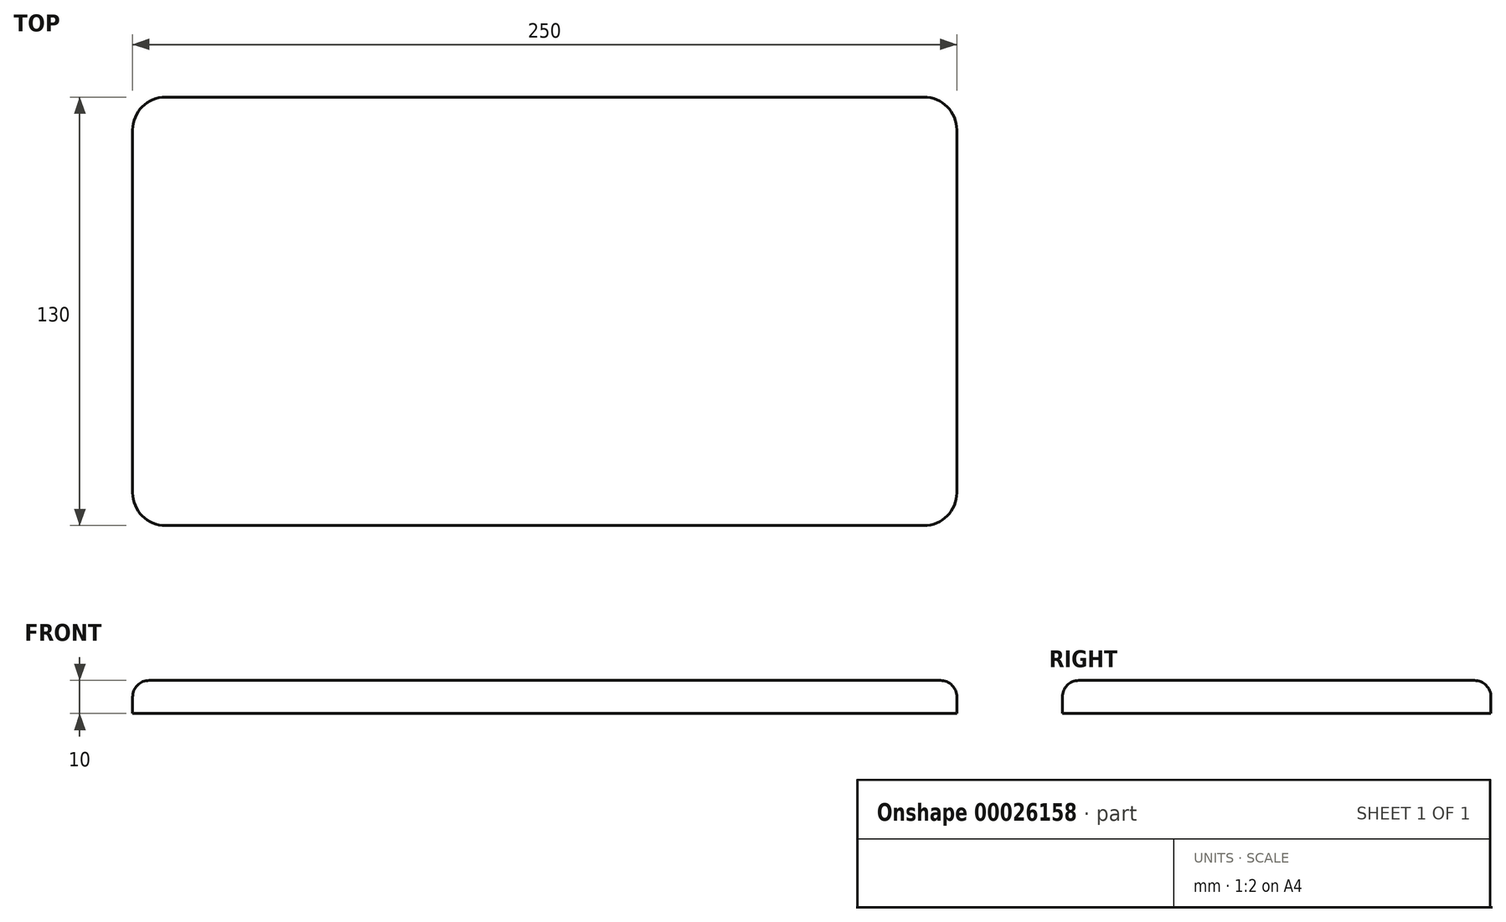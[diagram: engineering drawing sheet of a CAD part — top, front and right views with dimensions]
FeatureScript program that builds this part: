
annotation { "Feature Type Name" : "Feature", "Feature Type Description" : "" }
export const myFeature = defineFeature(function(context is Context, id is Id, definition is map)
    precondition{}
    {
        {
            var Q0;
            Q0=qCreatedBy(makeId("Top.planeOp"),FACE);
            var sketch = newSketch(context, id + "F0", { "sketchPlane" : qUnion([Q0])});
            skLineSegment(sketch, "E0.bottom", {"start": v(-167.36, 72.19) * mm, "end": v(82.64, 72.19) * mm});
            skLineSegment(sketch, "E0.top", {"start": v(-167.36, -57.81) * mm, "end": v(82.64, -57.81) * mm});
            skLineSegment(sketch, "E0.left", {"start": v(-167.36, 72.19) * mm, "end": v(-167.36, -57.81) * mm});
            skLineSegment(sketch, "E0.right", {"start": v(82.64, 72.19) * mm, "end": v(82.64, -57.81) * mm});
            skSolve(sketch);
        }
        {
            var Q0;
            Q0=makeQuery(id+"F0.imprint","IMPRINT",FACE,{"disambiguationData":[TD([[makeQuery(id+"F0.imprint","IMPRINT",EDGE,{"derivedFrom":sQuery(id+"F0.wireOp",EDGE,"E0.bottom")}),-1.0]])]});
            extrude(context, id + "F1", {"entities" : qUnion([Q0]), "depth" : 10 * mm});
        }
        {
            var Q0;
            Q0=makeQuery(id+"F1.opExtrude","SWEPT_EDGE",EDGE,{"disambiguationData":[OSD([sQuery(id+"F0.wireOp",EDGE,"E0.top"),sQuery(id+"F0.wireOp",EDGE,"E0.right")])]});
            var Q1;
            Q1=makeQuery(id+"F1.opExtrude","SWEPT_EDGE",EDGE,{"disambiguationData":[OSD([sQuery(id+"F0.wireOp",EDGE,"E0.bottom"),sQuery(id+"F0.wireOp",EDGE,"E0.right")])]});
            var Q2;
            Q2=makeQuery(id+"F1.opExtrude","SWEPT_EDGE",EDGE,{"disambiguationData":[OSD([sQuery(id+"F0.wireOp",EDGE,"E0.top"),sQuery(id+"F0.wireOp",EDGE,"E0.left")])]});
            var Q3;
            Q3=makeQuery(id+"F1.opExtrude","SWEPT_EDGE",EDGE,{"disambiguationData":[OSD([sQuery(id+"F0.wireOp",EDGE,"E0.bottom"),sQuery(id+"F0.wireOp",EDGE,"E0.left")])]});
            fillet(context, id + "F2", {"entities" : qUnion([Q0, Q1, Q2, Q3]), "radius" : 10 * mm, "tangentPropagation" : true, "allowEdgeOverflow" : false});
        }
        {
            var Q0;
            Q0=makeQuery(id+"F1.opExtrude","CAP_FACE",FACE,{"disambiguationData":[OSD([sQuery(id+"F0.wireOp",EDGE,"E0.bottom"),sQuery(id+"F0.wireOp",EDGE,"E0.top"),sQuery(id+"F0.wireOp",EDGE,"E0.left"),sQuery(id+"F0.wireOp",EDGE,"E0.right")])],"isStart":false});
            var sketch = newSketch(context, id + "F3", { "sketchPlane" : qUnion([Q0])});
            skLineSegment(sketch, "E1.bottom", {"start": v(-143.32, 58.74) * mm, "end": v(51.68, 58.74) * mm});
            skLineSegment(sketch, "E1.top", {"start": v(-143.32, -46.26) * mm, "end": v(51.68, -46.26) * mm});
            skLineSegment(sketch, "E1.left", {"start": v(-143.32, 58.74) * mm, "end": v(-143.32, -46.26) * mm});
            skLineSegment(sketch, "E1.right", {"start": v(51.68, 58.74) * mm, "end": v(51.68, -46.26) * mm});
            skSolve(sketch);
        }
        {
            var Q0;
            Q0=makeQuery(id+"F1.opExtrude","CAP_EDGE",EDGE,{"disambiguationData":[OSD([sQuery(id+"F0.wireOp",EDGE,"E0.top")])],"isStart":false});
            var Q1;
            Q1=makeQuery(id+"F1.opExtrude","CAP_EDGE",EDGE,{"disambiguationData":[OSD([sQuery(id+"F0.wireOp",EDGE,"E0.bottom")])],"isStart":false});
            var Q2;
            Q2=makeQuery(id+"F1.opExtrude","CAP_EDGE",EDGE,{"disambiguationData":[OSD([sQuery(id+"F0.wireOp",EDGE,"E0.left")])],"isStart":false});
            var Q3;
            Q3=makeQuery(id+"F1.opExtrude","CAP_EDGE",EDGE,{"disambiguationData":[OSD([sQuery(id+"F0.wireOp",EDGE,"E0.right")])],"isStart":false});
            fillet(context, id + "F4", {"entities" : qUnion([Q0, Q1, Q2, Q3]), "radius" : 5 * mm, "tangentPropagation" : true, "allowEdgeOverflow" : false});
        }
    });
